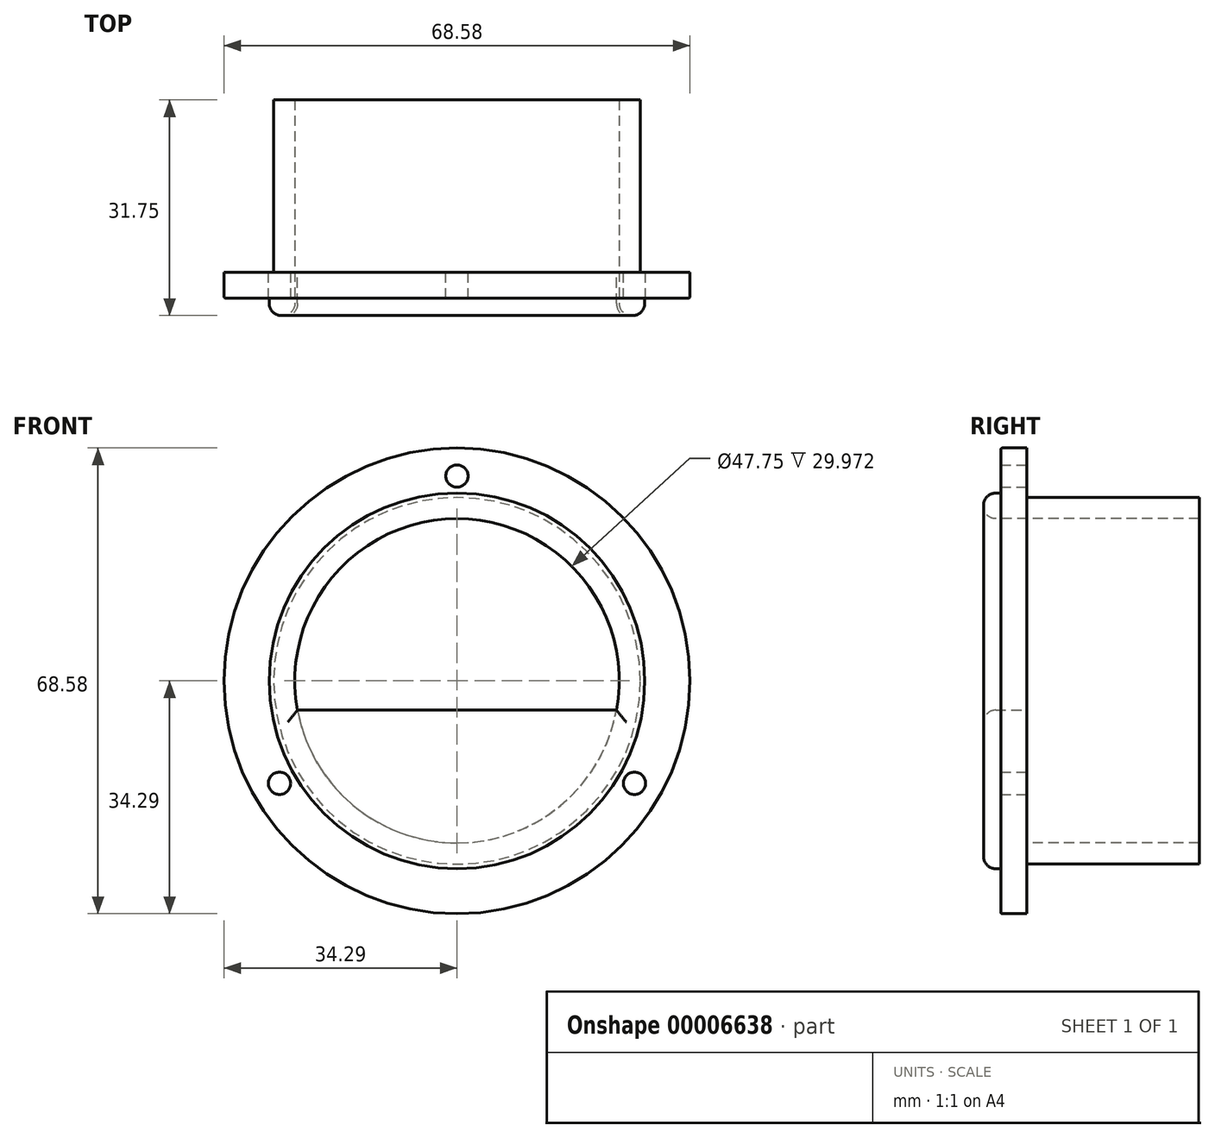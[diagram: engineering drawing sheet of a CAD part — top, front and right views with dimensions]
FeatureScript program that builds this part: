
annotation { "Feature Type Name" : "Feature", "Feature Type Description" : "" }
export const myFeature = defineFeature(function(context is Context, id is Id, definition is map)
    precondition{}
    {
        {
            var Q0;
            Q0=qCreatedBy(makeId("Front.planeOp"),FACE);
            var sketch = newSketch(context, id + "F0", { "sketchPlane" : qUnion([Q0])});
            skCircle(sketch, "E0", {"center": v(0, 0) * mm, "radius": 26.99 * mm});
            skCircle(sketch, "E1", {"center": v(0, 0) * mm, "radius": 30.16 * mm, "construction": true});
            skLineSegment(sketch, "E2", {"start": v(0, 43.94) * mm, "end": v(0, -44.02) * mm, "construction": true});
            skCircle(sketch, "E3", {"center": v(0, 30.16) * mm, "radius": 1.64 * mm});
            skCircle(sketch, "E4.1.0", {"center": v(-26.12, -15.08) * mm, "radius": 1.64 * mm});
            skCircle(sketch, "E4.2.0", {"center": v(26.12, -15.08) * mm, "radius": 1.64 * mm});
            skCircle(sketch, "E5", {"center": v(0, 0) * mm, "radius": 34.3 * mm});
            skCircle(sketch, "E6", {"center": v(0, 0) * mm, "radius": 27.65 * mm});
            skCircle(sketch, "E7", {"center": v(0, 0) * mm, "radius": 23.88 * mm});
            skLineSegment(sketch, "E8", {"start": v(-56.24, -4.32) * mm, "end": v(48.94, -4.32) * mm});
            skLineSegment(sketch, "E9", {"start": v(51.12, 23.88) * mm, "end": v(-48.79, 23.88) * mm, "construction": true});
            skSolve(sketch);
        }
        {
            var Q0;
            {var subQ0=sQuery(id+"F0.wireOp",EDGE,"E8");var subQ3=sQuery(id+"F0.wireOp",EDGE,"E0");var subQ6=makeQuery(id+"F0.imprint","INTERSECT",VERTEX,{"disambiguationData":[OD(0.0)],"derivedFrom":[subQ3,subQ0]});Q0=makeQuery(id+"F0.imprint","IMPRINT",FACE,{"disambiguationData":[TD([[makeQuery(id+"F0.imprint","IMPRINT",EDGE,{"disambiguationData":[TD([[subQ6,1.0]])],"derivedFrom":subQ3}),1.0]])]});}
            var Q1;
            {var subQ0=sQuery(id+"F0.wireOp",EDGE,"E8");var subQ3=sQuery(id+"F0.wireOp",EDGE,"E0");var subQ6=makeQuery(id+"F0.imprint","INTERSECT",VERTEX,{"disambiguationData":[OD(0.0)],"derivedFrom":[subQ3,subQ0]});Q1=makeQuery(id+"F0.imprint","IMPRINT",FACE,{"disambiguationData":[TD([[makeQuery(id+"F0.imprint","IMPRINT",EDGE,{"disambiguationData":[TD([[subQ6,-1.0]])],"derivedFrom":subQ3}),1.0]])]});}
            extrude(context, id + "F1", {"entities" : qUnion([Q0, Q1]), "oppositeDirection" : true, "depth" : 25.4 * mm});
        }
        {
            var Q0;
            Q0=makeQuery(id+"F0.imprint","IMPRINT",FACE,{"disambiguationData":[TD([[makeQuery(id+"F0.imprint","IMPRINT",EDGE,{"derivedFrom":sQuery(id+"F0.wireOp",EDGE,"E3")}),-1.0]])]});
            var Q1;
            {var subQ0=sQuery(id+"F0.wireOp",EDGE,"E8");var subQ3=sQuery(id+"F0.wireOp",EDGE,"E0");var subQ6=makeQuery(id+"F0.imprint","INTERSECT",VERTEX,{"disambiguationData":[OD(0.0)],"derivedFrom":[subQ3,subQ0]});Q1=makeQuery(id+"F0.imprint","IMPRINT",FACE,{"disambiguationData":[TD([[makeQuery(id+"F0.imprint","IMPRINT",EDGE,{"disambiguationData":[TD([[subQ6,1.0]])],"derivedFrom":subQ3}),-1.0]])]});}
            var Q2;
            {var subQ0=sQuery(id+"F0.wireOp",EDGE,"E8");var subQ3=sQuery(id+"F0.wireOp",EDGE,"E0");var subQ6=makeQuery(id+"F0.imprint","INTERSECT",VERTEX,{"disambiguationData":[OD(0.0)],"derivedFrom":[subQ3,subQ0]});Q2=makeQuery(id+"F0.imprint","IMPRINT",FACE,{"disambiguationData":[TD([[makeQuery(id+"F0.imprint","IMPRINT",EDGE,{"disambiguationData":[TD([[subQ6,1.0]])],"derivedFrom":subQ3}),1.0]])]});}
            var Q3;
            {var subQ0=sQuery(id+"F0.wireOp",EDGE,"E8");var subQ3=sQuery(id+"F0.wireOp",EDGE,"E0");var subQ6=makeQuery(id+"F0.imprint","INTERSECT",VERTEX,{"disambiguationData":[OD(0.0)],"derivedFrom":[subQ3,subQ0]});Q3=makeQuery(id+"F0.imprint","IMPRINT",FACE,{"disambiguationData":[TD([[makeQuery(id+"F0.imprint","IMPRINT",EDGE,{"disambiguationData":[TD([[subQ6,-1.0]])],"derivedFrom":subQ3}),-1.0]])]});}
            var Q4;
            Q4=makeQuery(id+"F0.imprint","IMPRINT",FACE,{"disambiguationData":[TD([[makeQuery(id+"F0.imprint","IMPRINT",EDGE,{"derivedFrom":sQuery(id+"F0.wireOp",EDGE,"E4.1.0")}),-1.0]])]});
            var Q5;
            {var subQ0=sQuery(id+"F0.wireOp",EDGE,"E8");var subQ3=sQuery(id+"F0.wireOp",EDGE,"E0");var subQ6=makeQuery(id+"F0.imprint","INTERSECT",VERTEX,{"disambiguationData":[OD(0.0)],"derivedFrom":[subQ3,subQ0]});Q5=makeQuery(id+"F0.imprint","IMPRINT",FACE,{"disambiguationData":[TD([[makeQuery(id+"F0.imprint","IMPRINT",EDGE,{"disambiguationData":[TD([[subQ6,-1.0]])],"derivedFrom":subQ3}),1.0]])]});}
            var Q6;
            {var subQ0=sQuery(id+"F0.wireOp",EDGE,"E8");var subQ1=sQuery(id+"F0.wireOp",EDGE,"E7");var subQ3=makeQuery(id+"F0.imprint","INTERSECT",VERTEX,{"disambiguationData":[OD(0.0)],"derivedFrom":[subQ1,subQ0]});Q6=makeQuery(id+"F0.imprint","IMPRINT",FACE,{"disambiguationData":[TD([[makeQuery(id+"F0.imprint","IMPRINT",EDGE,{"disambiguationData":[TD([[subQ3,-1.0]])],"derivedFrom":subQ1}),1.0]])]});}
            extrude(context, id + "F2", {"entities" : qUnion([Q0, Q1, Q2, Q3, Q4, Q5, Q6]), "operationType" : NewBodyOperationType.ADD, "depth" : 3.8 * mm});
        }
        {
            var Q0;
            {var subQ0=sQuery(id+"F0.wireOp",EDGE,"E8");var subQ3=sQuery(id+"F0.wireOp",EDGE,"E0");var subQ6=makeQuery(id+"F0.imprint","INTERSECT",VERTEX,{"disambiguationData":[OD(0.0)],"derivedFrom":[subQ3,subQ0]});Q0=makeQuery(id+"F0.imprint","IMPRINT",FACE,{"disambiguationData":[TD([[makeQuery(id+"F0.imprint","IMPRINT",EDGE,{"disambiguationData":[TD([[subQ6,1.0]])],"derivedFrom":subQ3}),-1.0]])]});}
            var Q1;
            {var subQ0=sQuery(id+"F0.wireOp",EDGE,"E8");var subQ3=sQuery(id+"F0.wireOp",EDGE,"E0");var subQ6=makeQuery(id+"F0.imprint","INTERSECT",VERTEX,{"disambiguationData":[OD(0.0)],"derivedFrom":[subQ3,subQ0]});Q1=makeQuery(id+"F0.imprint","IMPRINT",FACE,{"disambiguationData":[TD([[makeQuery(id+"F0.imprint","IMPRINT",EDGE,{"disambiguationData":[TD([[subQ6,1.0]])],"derivedFrom":subQ3}),1.0]])]});}
            var Q2;
            {var subQ0=sQuery(id+"F0.wireOp",EDGE,"E8");var subQ1=sQuery(id+"F0.wireOp",EDGE,"E7");var subQ3=makeQuery(id+"F0.imprint","INTERSECT",VERTEX,{"disambiguationData":[OD(0.0)],"derivedFrom":[subQ1,subQ0]});Q2=makeQuery(id+"F0.imprint","IMPRINT",FACE,{"disambiguationData":[TD([[makeQuery(id+"F0.imprint","IMPRINT",EDGE,{"disambiguationData":[TD([[subQ3,-1.0]])],"derivedFrom":subQ1}),1.0]])]});}
            var Q3;
            {var subQ0=sQuery(id+"F0.wireOp",EDGE,"E8");var subQ3=sQuery(id+"F0.wireOp",EDGE,"E0");var subQ6=makeQuery(id+"F0.imprint","INTERSECT",VERTEX,{"disambiguationData":[OD(0.0)],"derivedFrom":[subQ3,subQ0]});Q3=makeQuery(id+"F0.imprint","IMPRINT",FACE,{"disambiguationData":[TD([[makeQuery(id+"F0.imprint","IMPRINT",EDGE,{"disambiguationData":[TD([[subQ6,-1.0]])],"derivedFrom":subQ3}),1.0]])]});}
            var Q4;
            {var subQ0=sQuery(id+"F0.wireOp",EDGE,"E8");var subQ3=sQuery(id+"F0.wireOp",EDGE,"E0");var subQ6=makeQuery(id+"F0.imprint","INTERSECT",VERTEX,{"disambiguationData":[OD(0.0)],"derivedFrom":[subQ3,subQ0]});Q4=makeQuery(id+"F0.imprint","IMPRINT",FACE,{"disambiguationData":[TD([[makeQuery(id+"F0.imprint","IMPRINT",EDGE,{"disambiguationData":[TD([[subQ6,-1.0]])],"derivedFrom":subQ3}),-1.0]])]});}
            extrude(context, id + "F3", {"entities" : qUnion([Q0, Q1, Q2, Q3, Q4]), "operationType" : NewBodyOperationType.ADD, "depth" : 6.35 * mm});
        }
        {
            var Q0;
            Q0=makeQuery(id+"F2.opExtrude","CAP_EDGE",EDGE,{"disambiguationData":[OSD([sQuery(id+"F0.wireOp",EDGE,"E5")])],"isStart":false});
            fillet(context, id + "F4", {"entities" : qUnion([Q0]), "radius" : 0.25 * mm, "tangentPropagation" : true, "allowEdgeOverflow" : false});
        }
        {
            var Q0;
            Q0=makeQuery(id+"F3.opExtrude","CAP_EDGE",EDGE,{"disambiguationData":[OSD([sQuery(id+"F0.wireOp",EDGE,"E6")])],"isStart":false});
            var Q1;
            Q1=makeQuery(id+"F3.opExtrude","CAP_EDGE",EDGE,{"disambiguationData":[OSD([sQuery(id+"F0.wireOp",EDGE,"E7")])],"isStart":false});
            var Q2;
            Q2=makeQuery(id+"F3.opExtrude","CAP_EDGE",EDGE,{"disambiguationData":[OSD([sQuery(id+"F0.wireOp",EDGE,"E8")])],"isStart":false});
            fillet(context, id + "F5", {"entities" : qUnion([Q0, Q1, Q2]), "radius" : 1.78 * mm, "tangentPropagation" : true, "allowEdgeOverflow" : false});
        }
    });
